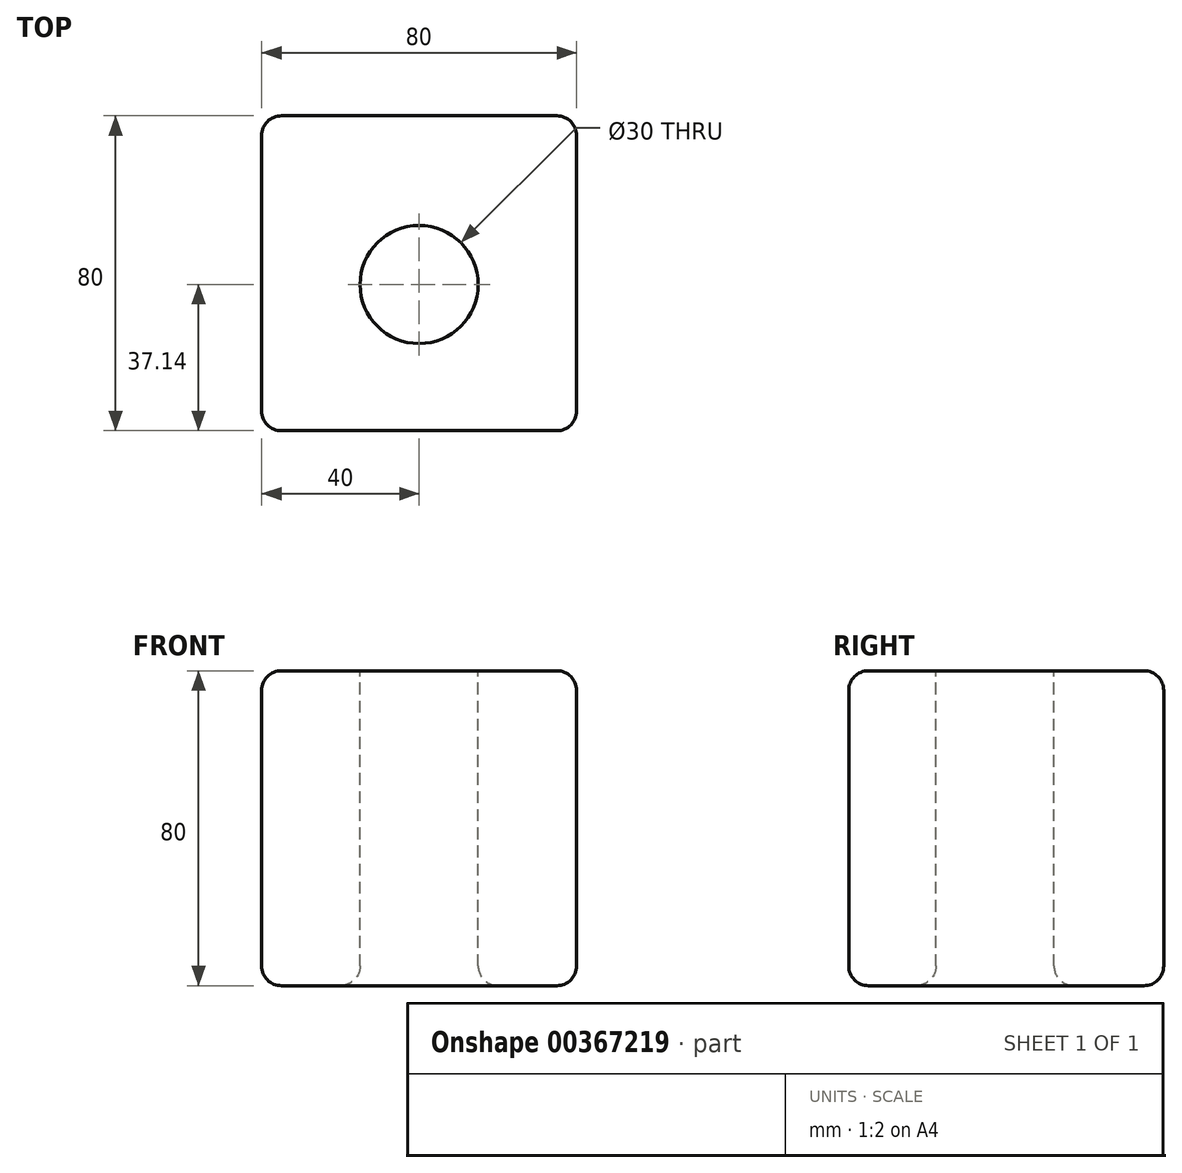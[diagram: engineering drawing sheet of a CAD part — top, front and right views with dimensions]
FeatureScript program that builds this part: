
annotation { "Feature Type Name" : "Feature", "Feature Type Description" : "" }
export const myFeature = defineFeature(function(context is Context, id is Id, definition is map)
    precondition{}
    {
        {
            var Q0;
            Q0=qCreatedBy(makeId("Top.planeOp"),FACE);
            var sketch = newSketch(context, id + "F0", { "sketchPlane" : qUnion([Q0])});
            skLineSegment(sketch, "E0.bottom", {"start": v(40, -37.14) * mm, "end": v(-40, -37.14) * mm});
            skLineSegment(sketch, "E0.top", {"start": v(40, 42.86) * mm, "end": v(-40, 42.86) * mm});
            skLineSegment(sketch, "E0.left", {"start": v(40, -37.14) * mm, "end": v(40, 42.86) * mm});
            skLineSegment(sketch, "E0.right", {"start": v(-40, -37.14) * mm, "end": v(-40, 42.86) * mm});
            skPoint(sketch, "E0.middle", {"position": v(0, 2.86) * mm});
            skSolve(sketch);
        }
        {
            var Q0;
            Q0=makeQuery(id+"F0.imprint","IMPRINT",FACE,{"disambiguationData":[TD([[makeQuery(id+"F0.imprint","IMPRINT",EDGE,{"derivedFrom":sQuery(id+"F0.wireOp",EDGE,"E0.bottom")}),-1.0]])]});
            extrude(context, id + "F1", {"entities" : qUnion([Q0]), "depth" : 80 * mm});
        }
        {
            var Q0;
            Q0=makeQuery(id+"F1.opExtrude","CAP_FACE",FACE,{"disambiguationData":[OSD([sQuery(id+"F0.wireOp",EDGE,"E0.bottom"),sQuery(id+"F0.wireOp",EDGE,"E0.top"),sQuery(id+"F0.wireOp",EDGE,"E0.left"),sQuery(id+"F0.wireOp",EDGE,"E0.right")])],"isStart":false});
            var sketch = newSketch(context, id + "F2", { "sketchPlane" : qUnion([Q0])});
            skCircle(sketch, "E1", {"center": v(0, 0) * mm, "radius": 15 * mm});
            skSolve(sketch);
        }
        {
            var Q0;
            Q0=makeQuery(id+"F2.imprint","IMPRINT",FACE,{"disambiguationData":[TD([[makeQuery(id+"F2.imprint","IMPRINT",EDGE,{"derivedFrom":sQuery(id+"F2.wireOp",EDGE,"E1")}),1.0]])]});
            extrude(context, id + "F3", {"entities" : qUnion([Q0]), "operationType" : NewBodyOperationType.REMOVE, "endBound" : BoundingType.THROUGH_ALL, "oppositeDirection" : true, "depth" : 25 * mm});
        }
        {
            var Q0;
            Q0=makeQuery(id+"F1.opExtrude","CAP_EDGE",EDGE,{"disambiguationData":[OSD([sQuery(id+"F0.wireOp",EDGE,"E0.top")])],"isStart":false});
            var Q1;
            Q1=makeQuery(id+"F1.opExtrude","CAP_EDGE",EDGE,{"disambiguationData":[OSD([sQuery(id+"F0.wireOp",EDGE,"E0.left")])],"isStart":false});
            var Q2;
            Q2=makeQuery(id+"F1.opExtrude","CAP_EDGE",EDGE,{"disambiguationData":[OSD([sQuery(id+"F0.wireOp",EDGE,"E0.right")])],"isStart":false});
            var Q3;
            Q3=makeQuery(id+"F1.opExtrude","CAP_EDGE",EDGE,{"disambiguationData":[OSD([sQuery(id+"F0.wireOp",EDGE,"E0.bottom")])],"isStart":false});
            var Q4;
            Q4=makeQuery(id+"F1.opExtrude","SWEPT_EDGE",EDGE,{"disambiguationData":[OSD([sQuery(id+"F0.wireOp",EDGE,"E0.bottom"),sQuery(id+"F0.wireOp",EDGE,"E0.right")])]});
            var Q5;
            Q5=makeQuery(id+"F1.opExtrude","SWEPT_EDGE",EDGE,{"disambiguationData":[OSD([sQuery(id+"F0.wireOp",EDGE,"E0.bottom"),sQuery(id+"F0.wireOp",EDGE,"E0.left")])]});
            var Q6;
            Q6=makeQuery(id+"F1.opExtrude","CAP_EDGE",EDGE,{"disambiguationData":[OSD([sQuery(id+"F0.wireOp",EDGE,"E0.bottom")])],"isStart":true});
            var Q7;
            Q7=makeQuery(id+"F1.opExtrude","SWEPT_EDGE",EDGE,{"disambiguationData":[OSD([sQuery(id+"F0.wireOp",EDGE,"E0.top"),sQuery(id+"F0.wireOp",EDGE,"E0.right")])]});
            var Q8;
            Q8=makeQuery(id+"F1.opExtrude","SWEPT_EDGE",EDGE,{"disambiguationData":[OSD([sQuery(id+"F0.wireOp",EDGE,"E0.top"),sQuery(id+"F0.wireOp",EDGE,"E0.left")])]});
            var Q9;
            Q9=makeQuery(id+"F1.opExtrude","CAP_EDGE",EDGE,{"disambiguationData":[OSD([sQuery(id+"F0.wireOp",EDGE,"E0.top")])],"isStart":true});
            var Q10;
            Q10=makeQuery(id+"F1.opExtrude","CAP_EDGE",EDGE,{"disambiguationData":[OSD([sQuery(id+"F0.wireOp",EDGE,"E0.right")])],"isStart":true});
            var Q11;
            Q11=makeQuery(id+"F1.opExtrude","CAP_EDGE",EDGE,{"disambiguationData":[OSD([sQuery(id+"F0.wireOp",EDGE,"E0.left")])],"isStart":true});
            var Q12;
            Q12=makeQuery(id+"F3.boolean.opBoolean","COPY",EDGE,{"derivedFrom":makeQuery(id+"F3.opExtrude","CAP_EDGE",EDGE,{"disambiguationData":[OSD([sQuery(id+"F2.wireOp",EDGE,"E1")])],"isStart":true})});
            var Q13;
            Q13=makeQuery(id+"F3.boolean.opBoolean","INTERSECT",EDGE,{"derivedFrom":[makeQuery(id+"F1.opExtrude","CAP_FACE",FACE,{"disambiguationData":[OSD([sQuery(id+"F0.wireOp",EDGE,"E0.bottom"),sQuery(id+"F0.wireOp",EDGE,"E0.top"),sQuery(id+"F0.wireOp",EDGE,"E0.left"),sQuery(id+"F0.wireOp",EDGE,"E0.right")])],"isStart":true}),makeQuery(id+"F3.opExtrude","SWEPT_FACE",FACE,{"disambiguationData":[OSD([sQuery(id+"F2.wireOp",EDGE,"E1")])]})]});
            fillet(context, id + "F4", {"entities" : qUnion([Q0, Q1, Q2, Q3, Q4, Q5, Q6, Q7, Q8, Q9, Q10, Q11, Q12, Q13]), "radius" : 5 * mm, "tangentPropagation" : true, "allowEdgeOverflow" : false});
        }
    });
